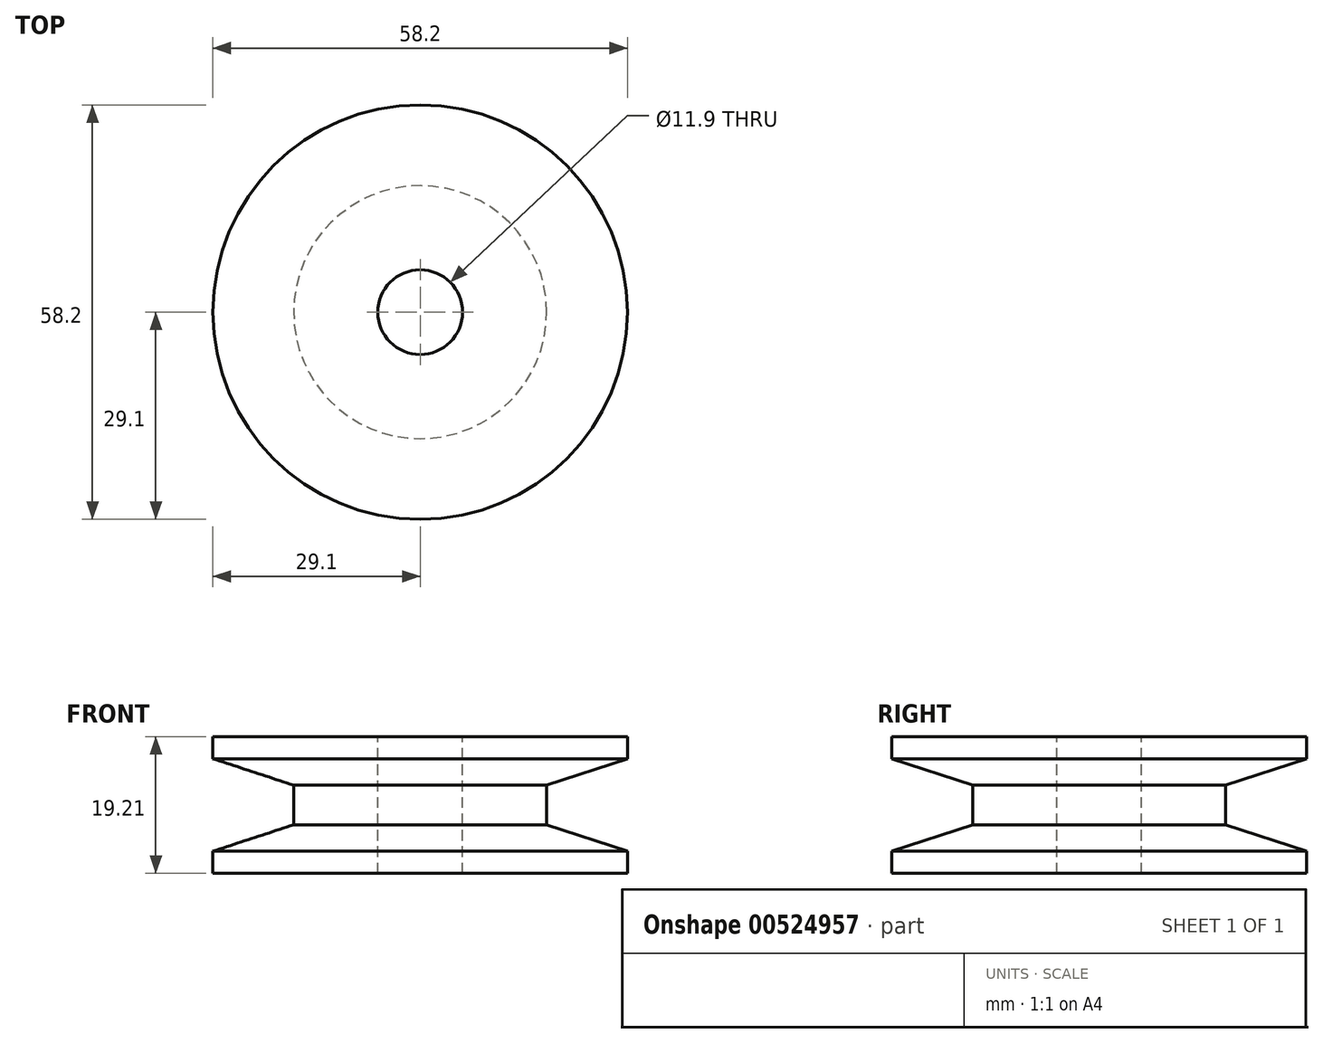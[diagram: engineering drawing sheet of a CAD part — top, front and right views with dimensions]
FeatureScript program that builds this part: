
annotation { "Feature Type Name" : "Feature", "Feature Type Description" : "" }
export const myFeature = defineFeature(function(context is Context, id is Id, definition is map)
    precondition{}
    {
        {
            var Q0;
            Q0=qCreatedBy(makeId("Front.planeOp"),FACE);
            var sketch = newSketch(context, id + "F0", { "sketchPlane" : qUnion([Q0])});
            skLineSegment(sketch, "E0", {"start": v(0, 6.83) * mm, "end": v(29.1, 6.83) * mm});
            skLineSegment(sketch, "E1", {"start": v(29.1, 6.83) * mm, "end": v(29.1, 3.73) * mm});
            skLineSegment(sketch, "E2", {"start": v(29.1, 3.73) * mm, "end": v(17.76, 0) * mm});
            skLineSegment(sketch, "E3", {"start": v(17.76, 0) * mm, "end": v(17.76, -5.55) * mm});
            skLineSegment(sketch, "E4", {"start": v(17.76, -5.55) * mm, "end": v(29.1, -9.27) * mm});
            skLineSegment(sketch, "E5", {"start": v(29.1, -9.27) * mm, "end": v(29.1, -12.37) * mm});
            skLineSegment(sketch, "E6", {"start": v(29.1, -12.37) * mm, "end": v(0, -12.37) * mm});
            skLineSegment(sketch, "E7", {"start": v(0, -12.37) * mm, "end": v(0, 6.83) * mm});
            skPoint(sketch, "E8.startSnap0", {"position": v(0, -2.77) * mm});
            skPoint(sketch, "E8.endSnap0", {"position": v(0, -2.77) * mm});
            skLineSegment(sketch, "E9", {"start": v(45.5, -2.77) * mm, "end": v(0, -2.77) * mm, "construction": true});
            skLineSegment(sketch, "E10", {"start": v(0, -26) * mm, "end": v(0, 20.6) * mm, "construction": true});
            skSolve(sketch);
        }
        {
            var Q0;
            Q0=makeQuery(id+"F0.imprint","IMPRINT",FACE,{"disambiguationData":[TD([[makeQuery(id+"F0.imprint","IMPRINT",EDGE,{"derivedFrom":sQuery(id+"F0.wireOp",EDGE,"E0")}),-1.0]])]});
            var Q1;
            Q1=sQuery(id+"F0.wireOp",EDGE,"E10");
            revolve(context, id + "F1", {"entities" : qUnion([Q0]), "axis" : qUnion([Q1]), "revolveType" : RevolveType.FULL});
        }
        {
            var Q0;
            Q0=makeQuery(id+"F1.opRevolve","SWEPT_FACE",FACE,{"disambiguationData":[OSD([sQuery(id+"F0.wireOp",EDGE,"E0")])]});
            var sketch = newSketch(context, id + "F2", { "sketchPlane" : qUnion([Q0])});
            skCircle(sketch, "E11", {"center": v(0, 0) * mm, "radius": 5.95 * mm});
            skSolve(sketch);
        }
        {
            var Q0;
            Q0 = qSketchRegion(id + "F2", true);
            extrude(context, id + "F3", {"entities" : qUnion([Q0]), "operationType" : NewBodyOperationType.REMOVE, "endBound" : BoundingType.THROUGH_ALL, "oppositeDirection" : true, "depth" : 25.4 * mm, "offsetDistance" : 25.4 * mm});
        }
    });
